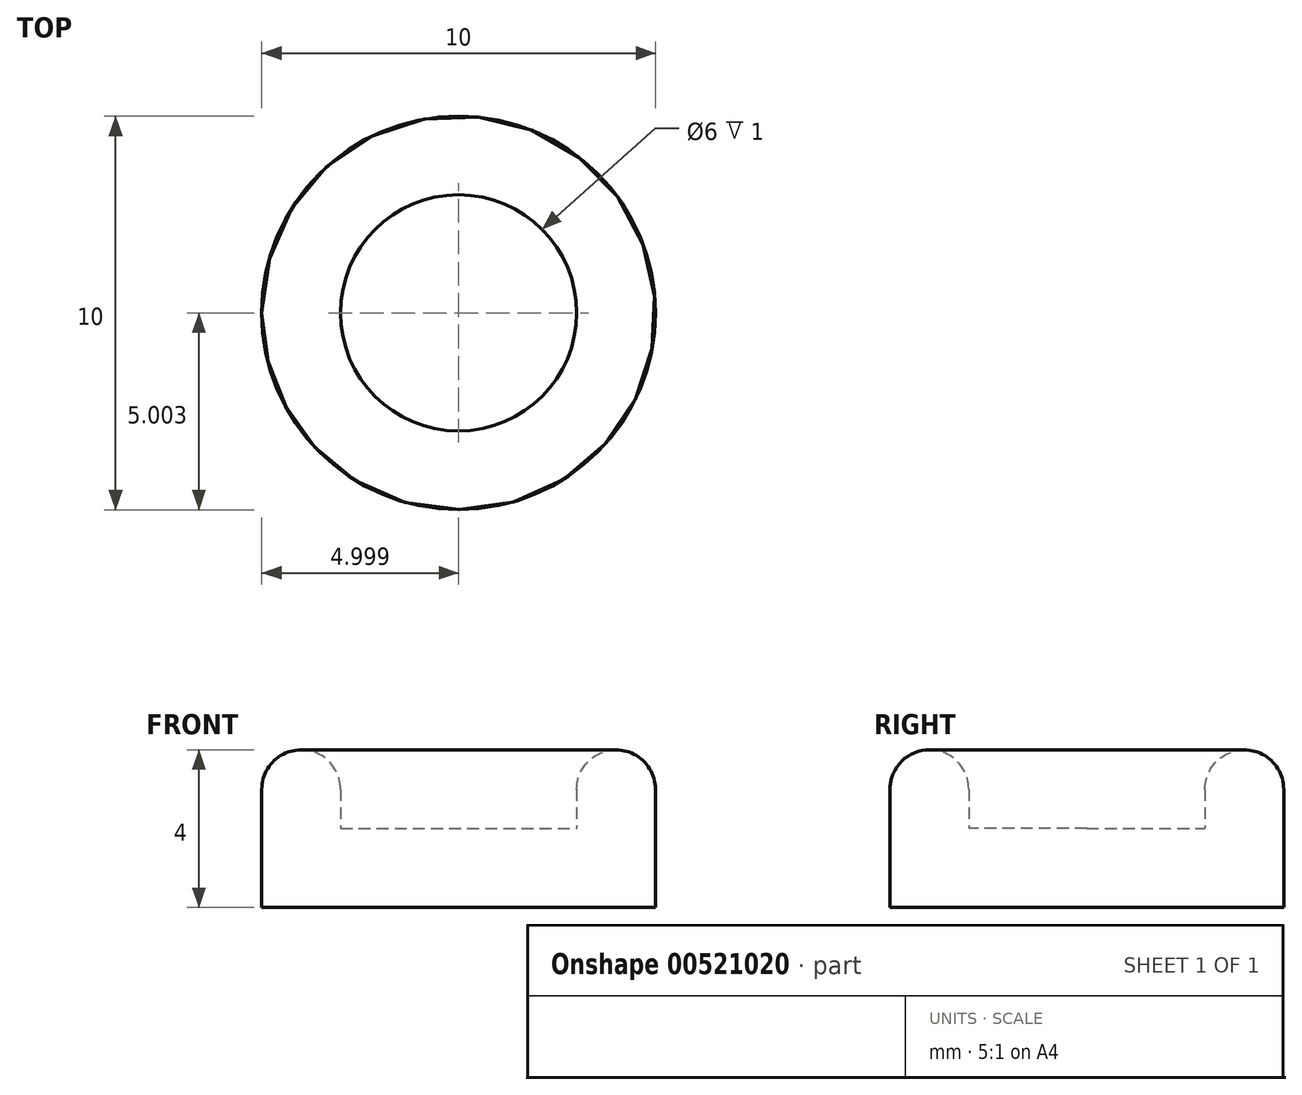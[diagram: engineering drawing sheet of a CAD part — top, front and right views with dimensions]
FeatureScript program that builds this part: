
annotation { "Feature Type Name" : "Feature", "Feature Type Description" : "" }
export const myFeature = defineFeature(function(context is Context, id is Id, definition is map)
    precondition{}
    {
        {
            var Q0;
            Q0=qCreatedBy(makeId("Top.planeOp"),FACE);
            var sketch = newSketch(context, id + "F0", { "sketchPlane" : qUnion([Q0])});
            skCircle(sketch, "E0", {"center": v(-49.26, -16.53) * mm, "radius": 5 * mm});
            skCircle(sketch, "E1", {"center": v(-49.26, -16.53) * mm, "radius": 3 * mm});
            skSolve(sketch);
        }
        {
            var Q0;
            Q0=makeQuery(id+"F0.imprint","IMPRINT",FACE,{"disambiguationData":[TD([[makeQuery(id+"F0.imprint","IMPRINT",EDGE,{"derivedFrom":sQuery(id+"F0.wireOp",EDGE,"E0")}),1.0]])]});
            extrude(context, id + "F1", {"entities" : qUnion([Q0]), "depth" : 5 * mm, "offsetDistance" : 25 * mm});
        }
        {
            var Q0;
            Q0 = qSketchRegion(id + "F0", true);
            var Q1;
            Q1=makeQuery(id+"F0.imprint","IMPRINT",FACE,{"disambiguationData":[TD([[makeQuery(id+"F0.imprint","IMPRINT",EDGE,{"derivedFrom":sQuery(id+"F0.wireOp",EDGE,"E1")}),1.0]])]});
            extrude(context, id + "F2", {"entities" : qUnion([Q0, Q1]), "operationType" : NewBodyOperationType.ADD, "depth" : 2 * mm, "offsetDistance" : 25 * mm});
        }
        {
            var Q0;
            Q0=makeQuery(id+"F1.opExtrude","CAP_EDGE",EDGE,{"disambiguationData":[OSD([sQuery(id+"F0.wireOp",EDGE,"E0")])],"isStart":false});
            fillet(context, id + "F3", {"entities" : qUnion([Q0]), "radius" : 2 * mm, "tangentPropagation" : true, "allowEdgeOverflow" : false});
        }
        {
            var Q0;
            Q0=makeQuery(id+"F3.opFillet","BLEND_EDGE",EDGE,{"blendedFrom":[makeQuery(id+"F1.opExtrude","CAP_EDGE",EDGE,{"disambiguationData":[OSD([sQuery(id+"F0.wireOp",EDGE,"E0")])],"isStart":false}),makeQuery(id+"F1.opExtrude","SWEPT_FACE",FACE,{"disambiguationData":[OSD([sQuery(id+"F0.wireOp",EDGE,"E1")])]})],"blendedInto":[makeQuery(id+"F1.opExtrude","SWEPT_FACE",FACE,{"disambiguationData":[OSD([sQuery(id+"F0.wireOp",EDGE,"E1")])]})]});
            fillet(context, id + "F4", {"entities" : qUnion([Q0]), "radius" : 1 * mm, "tangentPropagation" : true, "allowEdgeOverflow" : false});
        }
    });
